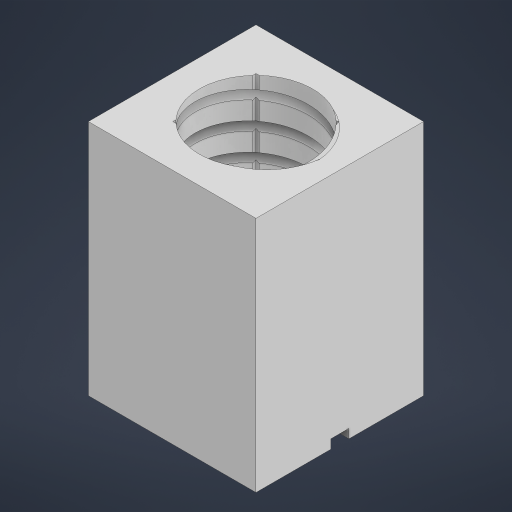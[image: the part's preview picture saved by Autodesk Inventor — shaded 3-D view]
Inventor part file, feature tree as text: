
AUTODESK INVENTOR PART (.ipt)
format: ipt  version: 2024.1 (Build 281209000, 209)  size: 1,022,464 bytes
history: native  units: mm
features: sketch x6, projected_geometry x6, extrude x5, helix x1
ambient origin geometry x8: Origin, YZ Plane, XZ Plane, XY Plane, X Axis, Y Axis, Z Axis, Center Point
bodies: Solid1 (feature_tree)
feature tree (18):
  extrude  "Extrusion1"  Depth=15.0mm
  extrude  "Extrusion2"  Depth=2.0mm TaperAngle=0.0deg
  extrude  "Extrusion3"  Depth=18.36mm
  helix  "Coil1"  [1 undecoded]
  extrude  "Extrusion4"  Depth=50.0mm TaperAngle=0.0deg
  extrude  "Extrusion5"  Depth=2.5mm
  sketch  "Sketch1"  dims[d0=15.0mm d1=15.0mm]
  sketch  "Sketch2"  dims[d2=37.0mm d3=2.0mm d4=0.0mm]
  projected_geometry  "Projected Loop1"
  sketch  "Sketch3"  dims[d6=18.36mm d7=18.36mm d8=0.4mm d9=0.0mm]
  projected_geometry  "Projected Loop2"
  sketch  "Sketch4"  dims[d10=25.0mm d11=50.0mm d12=0.0mm]
  sketch  "Sketch5"  dims[d13=60.0deg d14=2.5mm]
  projected_geometry  "Projected Loop3"
  projected_geometry  "Projected Loop4"
  projected_geometry  "Projected Loop5"
  projected_geometry  "Projected Loop6"
  sketch  "Sketch6"  dims[d15=2.0mm d16=6.0mm d17=10.0mm d18=100.0mm d19=0.0mm d20=90.0deg d21=90.0deg d22=0.0mm d23=0.0mm d24=21.0mm d25=50.0mm d26=0.0mm d27=4.0mm d28=10.0mm d29=0.0mm]
note: 1 required parameter value undecoded (feature->parameter linkage not recoverable at this tier; creation-order binding heuristic only, values carry confidence <= 0.55)
